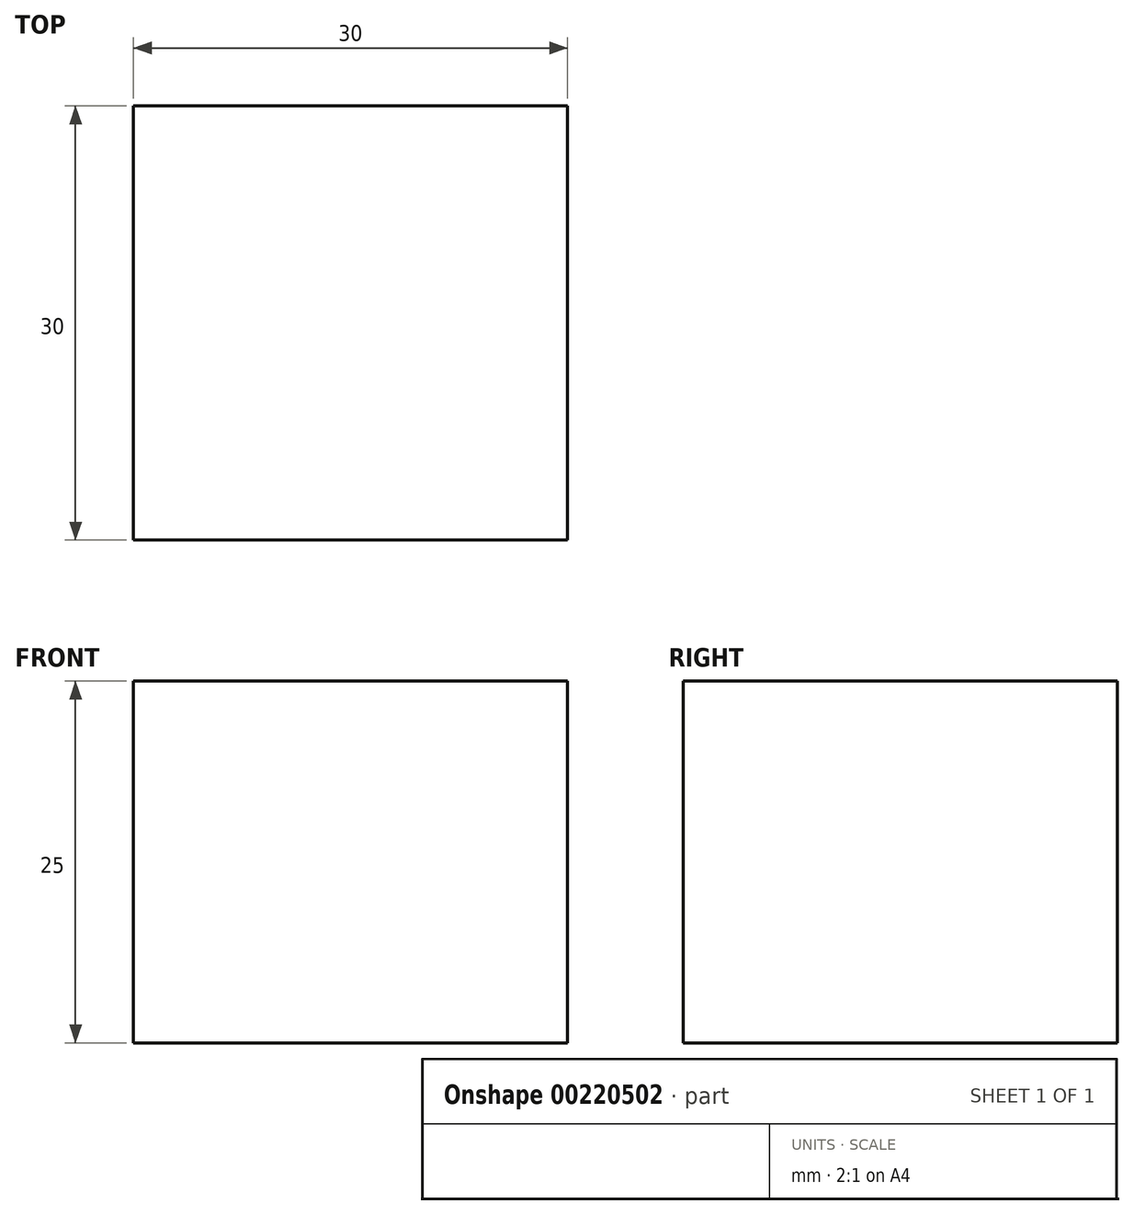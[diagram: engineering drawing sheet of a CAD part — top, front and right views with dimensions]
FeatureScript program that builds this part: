
annotation { "Feature Type Name" : "Feature", "Feature Type Description" : "" }
export const myFeature = defineFeature(function(context is Context, id is Id, definition is map)
    precondition{}
    {
        {
            var Q0;
            Q0=qCreatedBy(makeId("Top.planeOp"),FACE);
            var sketch = newSketch(context, id + "F0", { "sketchPlane" : qUnion([Q0])});
            skLineSegment(sketch, "E0.bottom", {"start": v(-14.55, 15) * mm, "end": v(15.45, 15) * mm});
            skLineSegment(sketch, "E0.top", {"start": v(-14.55, -15) * mm, "end": v(15.45, -15) * mm});
            skLineSegment(sketch, "E0.left", {"start": v(-14.55, 15) * mm, "end": v(-14.55, -15) * mm});
            skLineSegment(sketch, "E0.right", {"start": v(15.45, 15) * mm, "end": v(15.45, -15) * mm});
            skSolve(sketch);
        }
        {
            var Q0;
            Q0 = qSketchRegion(id + "F0", true);
            extrude(context, id + "F1", {"entities" : qUnion([Q0]), "depth" : 25 * mm});
        }
    });
